# Revit family: Plymold-Essentials-X_Series-Table_Base-
name_source: partatom
category: Furniture
units: mm (PartAtom-declared; Revit-internal decimal feet)

## family parameters
Always vertical = Yes
Cut with Voids When Loaded = No
OmniClass Number = 23.40.20.00
OmniClass Title = General Furniture and Specialties
Render Appearance Source = Family Geometry
Room Calculation Point = No
Shared = No
Work Plane-Based = No

## types (8) — shared parameters
Assembly Code = E2020200
BASE MATERIAL = PLY - Onyx Black Powdercoat
Brand = Table Bases
Default Elevation = 0"
GLIDES MATERIAL = PLY - Plastic Black
Keynote = 12500
Manufacturer = Plymold
Product Documentation Link = https://plymold.com
Revit Model Built By = https://www.servex-us.com
Sustainability = https://plymold.com
Type Comments = Tables
URL = https://plymold.com
zero-valued in all types: Cost

## per-type parameters (varying)
| type | Depth | Description | Height | Width |
| 7162230 | 22" | X Series Table Base Dining Height - 22"W x 22"D x 30”H | 30" | 22" |
| 7162330 | 22" | X Series Table Base Dining Height - 30"W x 22"D x 30”H | 30" | 30" |
| 7162430 | 30" | X Series Table Base Dining Height - 30"W x 30"D x 30”H | 30" | 30" |
| 7162530 | 36" | X Series Table Base Dining Height - 36"W x 36"D x 30”H | 30" | 36" |
| 7162242 | 22" | X Series Table Base Dining Height - 22"W x 22"D x 42”H | 42" | 22" |
| 7162342 | 22" | X Series Table Base Dining Height - 30"W x 22"D x 42”H | 42" | 30" |
| 7162442 | 30" | X Series Table Base Dining Height - 30"W x 30"D x 42”H | 42" | 30" |
| 7162542 | 36" | X Series Table Base Dining Height - 36"W x 36"D x 42”H | 42" | 36" |

note: column(s) folded — value = type name in every type: Model

## geometry (parser evidence)
native form markers: Sweep x5
no freeform markers — native parametric forms only
